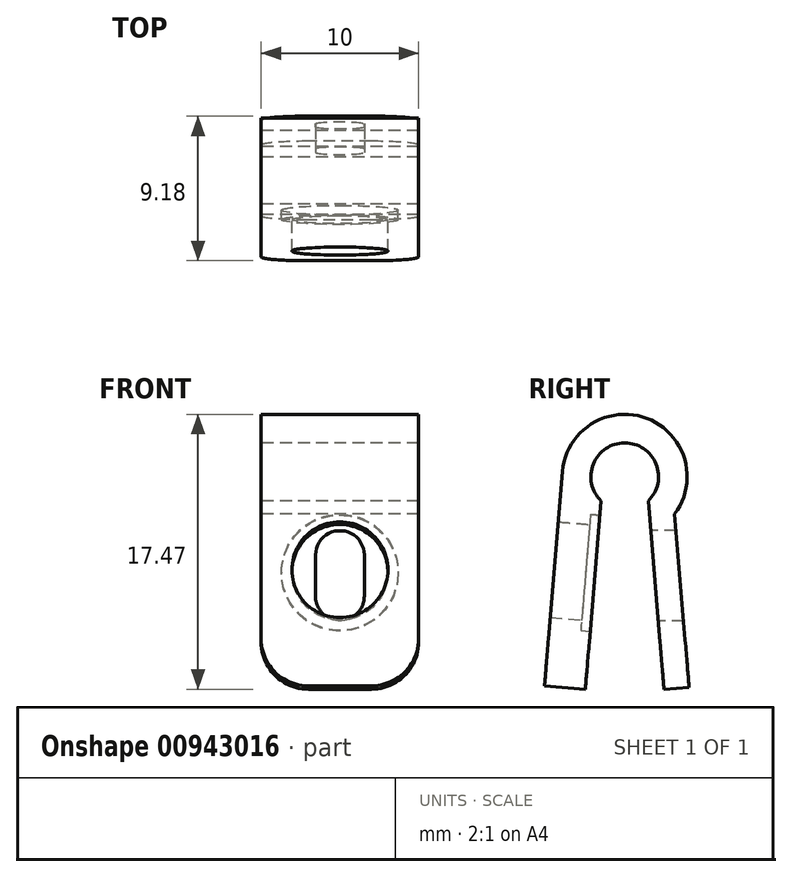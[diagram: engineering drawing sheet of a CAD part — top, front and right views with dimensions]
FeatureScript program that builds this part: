
annotation { "Feature Type Name" : "Feature", "Feature Type Description" : "" }
export const myFeature = defineFeature(function(context is Context, id is Id, definition is map)
    precondition{}
    {
        {
            var Q0;
            Q0=qCreatedBy(makeId("Right.planeOp"),FACE);
            var sketch = newSketch(context, id + "F0", { "sketchPlane" : qUnion([Q0])});
            skArc(sketch, "E0", {"start": v(1.5, -1.54) * mm, "mid": v(0, 2.15) * mm, "end": v(-1.5, -1.54) * mm});
            skLineSegment(sketch, "E1", {"start": v(-1.5, -1.54) * mm, "end": v(-2.5, -13.5) * mm});
            skLineSegment(sketch, "E2", {"start": v(1.5, -1.54) * mm, "end": v(2.5, -13.5) * mm});
            skLineSegment(sketch, "E3", {"start": v(-2.5, -13.5) * mm, "end": v(-5.1, -13.28) * mm});
            skLineSegment(sketch, "E4", {"start": v(-5.1, -13.28) * mm, "end": v(-3.95, 0.33) * mm});
            skArc(sketch, "E5", {"start": v(-3.95, 0.33) * mm, "mid": v(1.4, 3.7) * mm, "end": v(3.18, -2.38) * mm});
            skLineSegment(sketch, "E6.MirrorCS", {"start": v(4.1, -13.37) * mm, "end": v(3.18, -2.38) * mm});
            skLineSegment(sketch, "E7.MirrorCS", {"start": v(2.5, -13.5) * mm, "end": v(4.1, -13.37) * mm});
            skSolve(sketch);
        }
        {
            var Q0;
            Q0 = qSketchRegion(id + "F0", true);
            extrude(context, id + "F1", {"entities" : qUnion([Q0]), "depth" : 10 * mm, "offsetDistance" : 25 * mm});
        }
        {
            var Q0;
            Q0=qCreatedBy(makeId("Front.planeOp"),FACE);
            var sketch = newSketch(context, id + "F2", { "sketchPlane" : qUnion([Q0])});
            skPoint(sketch, "E8", {"position": v(5, -6.28) * mm});
            skPoint(sketch, "E9", {"position": v(5, -13.37) * mm});
            skLineSegment(sketch, "E10", {"start": v(5, -4.97) * mm, "end": v(5, -7.6) * mm, "construction": true});
            skArc(sketch, "E11.0.startCap", {"start": v(3.45, -4.97) * mm, "mid": v(5, -3.42) * mm, "end": v(6.55, -4.97) * mm});
            skArc(sketch, "E11.0.endCap", {"start": v(6.55, -7.6) * mm, "mid": v(5, -9.14) * mm, "end": v(3.45, -7.6) * mm});
            skLineSegment(sketch, "E11.0.left", {"start": v(6.55, -4.97) * mm, "end": v(6.55, -7.6) * mm});
            skLineSegment(sketch, "E11.0.right", {"start": v(3.45, -4.97) * mm, "end": v(3.45, -7.6) * mm});
            skSolve(sketch);
        }
        {
            var Q0;
            Q0 = qSketchRegion(id + "F2", true);
            extrude(context, id + "F3", {"entities" : qUnion([Q0]), "operationType" : NewBodyOperationType.REMOVE, "oppositeDirection" : true, "depth" : 25 * mm, "offsetDistance" : 25 * mm});
        }
        {
            var Q0;
            Q0=makeQuery(id+"F1.opExtrude","SWEPT_FACE",FACE,{"disambiguationData":[OSD([sQuery(id+"F0.wireOp",EDGE,"E1")])]});
            var sketch = newSketch(context, id + "F4", { "sketchPlane" : qUnion([Q0])});
            skPoint(sketch, "E12", {"position": v(-5, -6.26) * mm});
            skPoint(sketch, "E12.positionSnap0", {"position": v(-5, -13.66) * mm});
            skSolve(sketch);
        }
        {
            var Q0;
            Q0=sQuery(id+"F4.wireOp",VERTEX,"E12");
            var Q1;
            Q1=makeQuery(id+"F1.opExtrude","SWEPT_BODY",BODY,{"disambiguationData":[OSD([sQuery(id+"F0.wireOp",EDGE,"E0"),sQuery(id+"F0.wireOp",EDGE,"E1"),sQuery(id+"F0.wireOp",EDGE,"E2"),sQuery(id+"F0.wireOp",EDGE,"E3"),sQuery(id+"F0.wireOp",EDGE,"E4"),sQuery(id+"F0.wireOp",EDGE,"E5"),sQuery(id+"F0.wireOp",EDGE,"E6.MirrorCS"),sQuery(id+"F0.wireOp",EDGE,"E7.MirrorCS")])]});
            hole(context, id + "F5", {"style" : HoleStyle.C_BORE, "endStyle" : HoleEndStyle.THROUGH, "holeDiameter" : 6.1 * mm, "cBoreDiameter" : 7.4 * mm, "cBoreDepth" : 0.6 * mm, "majorDiameter" : 5 * mm, "isTappedThrough" : true, "tappedDepth" : 12 * mm, "tapClearance" : 3, "locations" : qUnion([Q0]), "scope" : qUnion([Q1])});
        }
        {
            var Q0;
            Q0=makeQuery(id+"F1.opExtrude","CAP_EDGE",EDGE,{"disambiguationData":[OSD([sQuery(id+"F0.wireOp",EDGE,"E3")])],"isStart":true});
            var Q1;
            Q1=makeQuery(id+"F1.opExtrude","CAP_EDGE",EDGE,{"disambiguationData":[OSD([sQuery(id+"F0.wireOp",EDGE,"E3")])],"isStart":false});
            var Q2;
            Q2=makeQuery(id+"F1.opExtrude","CAP_EDGE",EDGE,{"disambiguationData":[OSD([sQuery(id+"F0.wireOp",EDGE,"E7.MirrorCS")])],"isStart":false});
            var Q3;
            Q3=makeQuery(id+"F1.opExtrude","CAP_EDGE",EDGE,{"disambiguationData":[OSD([sQuery(id+"F0.wireOp",EDGE,"E7.MirrorCS")])],"isStart":true});
            fillet(context, id + "F6", {"entities" : qUnion([Q0, Q1, Q2, Q3]), "radius" : 3 * mm, "tangentPropagation" : true, "allowEdgeOverflow" : false});
        }
    });
